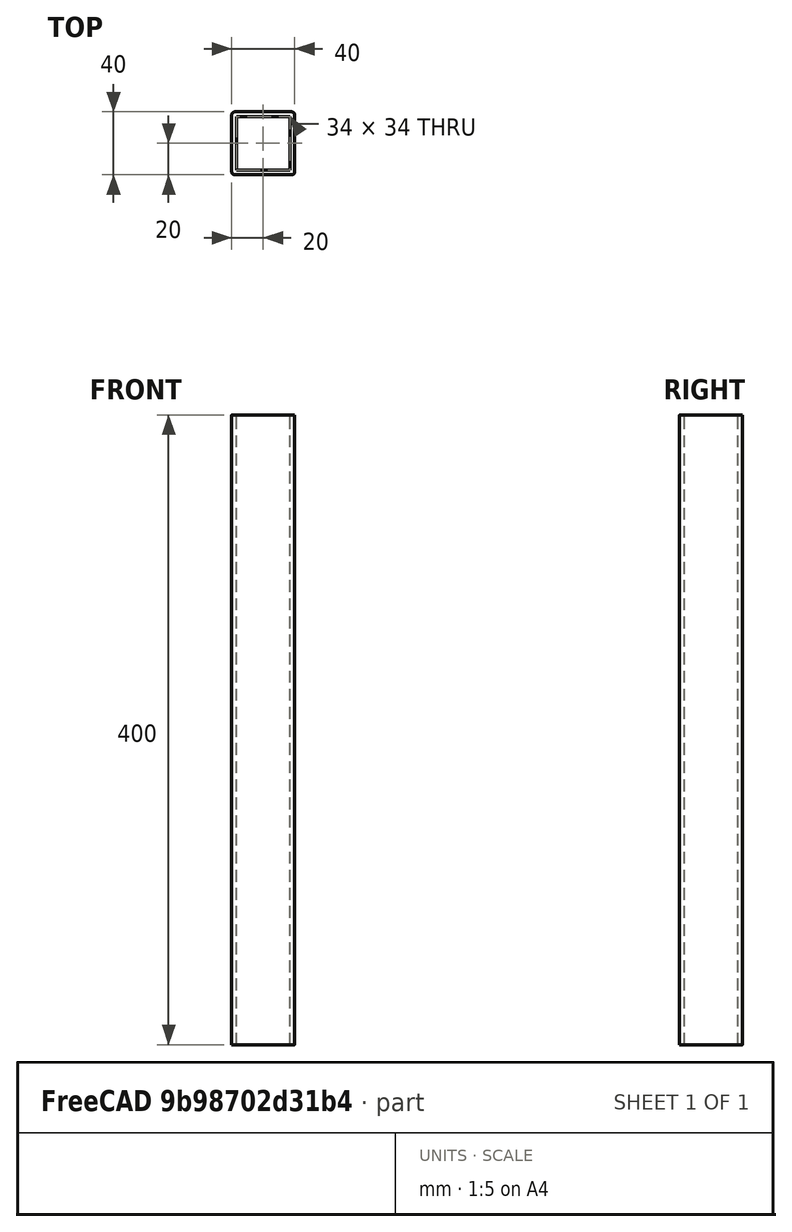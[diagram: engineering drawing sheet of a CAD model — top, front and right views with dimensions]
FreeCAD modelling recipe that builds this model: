
FCSTD DOCUMENT  (FreeCAD 1.0R39319 (Git))
Label: steel-profile-40x40x400
License: All rights reserved
LicenseURL: http://en.wikipedia.org/wiki/All_rights_reserved
objects: Sketcher::SketchObject×1, PartDesign::Pad×1, PartDesign::Body×1, App::Part×1
note: 6 computed .brp shape members not serialized (recipe doc carries the construction recipe); baked Part::Feature solids carry a one-line shape summary decoded from their .brp

FEATURE [Sketcher::SketchObject] Sketch
  ArcFitTolerance = 1e-06
  AttachmentSupport = -> [XY_Plane001]
  FullyConstrained = true
  MakeInternals = false
  MapMode = 5
  sketch-geometry (18):
    g0: LineSegment StartX=2 StartY=-9e-16 StartZ=0 EndX=38 EndY=-9e-16 EndZ=0
    g1: LineSegment StartX=40 StartY=2 StartZ=0 EndX=40 EndY=38 EndZ=0
    g2: LineSegment StartX=38 StartY=40 StartZ=0 EndX=2 EndY=40 EndZ=0
    g3: LineSegment StartX=-1.3e-15 StartY=38 StartZ=0 EndX=-1.3e-15 EndY=2 EndZ=0
    g4: ArcOfCircle CenterX=2 CenterY=2 CenterZ=0 NormalX=0 NormalY=0 NormalZ=1 AngleXU=0 Radius=2 StartAngle=3.14159 EndAngle=4.71239
    g5: ArcOfCircle CenterX=38 CenterY=2 CenterZ=0 NormalX=0 NormalY=0 NormalZ=1 AngleXU=0 Radius=2 StartAngle=4.71239 EndAngle=6.28319
    g6: ArcOfCircle CenterX=38 CenterY=38 CenterZ=0 NormalX=0 NormalY=0 NormalZ=1 AngleXU=0 Radius=2 StartAngle=0 EndAngle=1.5708
    g7: ArcOfCircle CenterX=2 CenterY=38 CenterZ=0 NormalX=0 NormalY=0 NormalZ=1 AngleXU=0 Radius=2 StartAngle=1.5708 EndAngle=3.14159
    g8: LineSegment StartX=3 StartY=3 StartZ=0 EndX=37 EndY=3 EndZ=0
    g9: LineSegment StartX=37 StartY=3 StartZ=0 EndX=37 EndY=37 EndZ=0
    g10: LineSegment StartX=37 StartY=37 StartZ=0 EndX=3 EndY=37 EndZ=0
    g11: LineSegment StartX=3 StartY=37 StartZ=0 EndX=3 EndY=3 EndZ=0
    g12: LineSegment [constr] StartX=2 StartY=2 StartZ=0 EndX=3 EndY=3 EndZ=0
    g13: LineSegment [constr] StartX=38 StartY=2 StartZ=0 EndX=37 EndY=3 EndZ=0
    g14: LineSegment [constr] StartX=38 StartY=38 StartZ=0 EndX=37 EndY=37 EndZ=0
    g15: LineSegment [constr] StartX=2 StartY=38 StartZ=0 EndX=3 EndY=37 EndZ=0
    g16: GeomPoint [constr] X=-1.6e-15 Y=-1.1e-15 Z=0
    g17: GeomPoint [constr] X=40 Y=40 Z=0
  constraints (43):
    c: Tangent(g0,g4) = -1.5708
    c: Tangent(g0,g5) = -1.5708
    c: Tangent(g1,g5) = -1.5708
    c: Tangent(g1,g6) = -1.5708
    c: Tangent(g2,g6) = -1.5708
    c: Tangent(g2,g7) = -1.5708
    c: Tangent(g3,g7) = -1.5708
    c: Tangent(g3,g4) = -1.5708
    c: Horizontal(g0)
    c: Horizontal(g2)
    c: Vertical(g1)
    c: Vertical(g3)
    c: Equal(g4,g5)
    c: Equal(g5,g6)
    c: Equal(g6,g7)
    c: Coincident(g8,g9)
    c: Coincident(g9,g10)
    c: Coincident(g10,g11)
    c: Coincident(g11,g8)
    c: Horizontal(g8)
    c: Horizontal(g10)
    c: Vertical(g9)
    c: Vertical(g11)
    c: Coincident(g12,g4)
    c: Coincident(g12,g8)
    c: Coincident(g13,g5)
    c: Coincident(g13,g9)
    c: Coincident(g14,g6)
    c: Coincident(g14,g10)
    c: Coincident(g15,g7)
    c: Coincident(g15,g11)
    c: Perpendicular(g12,g13)
    c: Perpendicular(g13,g14)
    c: Perpendicular(g14,g15)
    c: PointOnObject(g16,g0)
    c: PointOnObject(g16,g3)
    c: PointOnObject(g17,g1)
    c: PointOnObject(g17,g2)
    c: Distance(g1,g3) = 40
    c: Distance(g0,g2) = 40
    c: Radius(g5) = 2
    c: Distance(g8,g0) = 3
    c: Coincident(g16,g-1)
FEATURE [PartDesign::Pad] Pad
  Direction = (0,0,1)
  Length = 400
  Length2 = 10
  Profile = -> Sketch
  ReferenceAxis = -> Sketch [N_Axis]
  Suppressed = false
  Type = 0
FEATURE [PartDesign::Body] Body
  AllowCompound = false
  Group = -> [Sketch,Pad]
  Origin = -> Origin001
  Tip = -> Pad
FEATURE [App::Part] Part  label="steel-profile-40x40x400"
  Group = -> [Body]
  Origin = -> Origin
